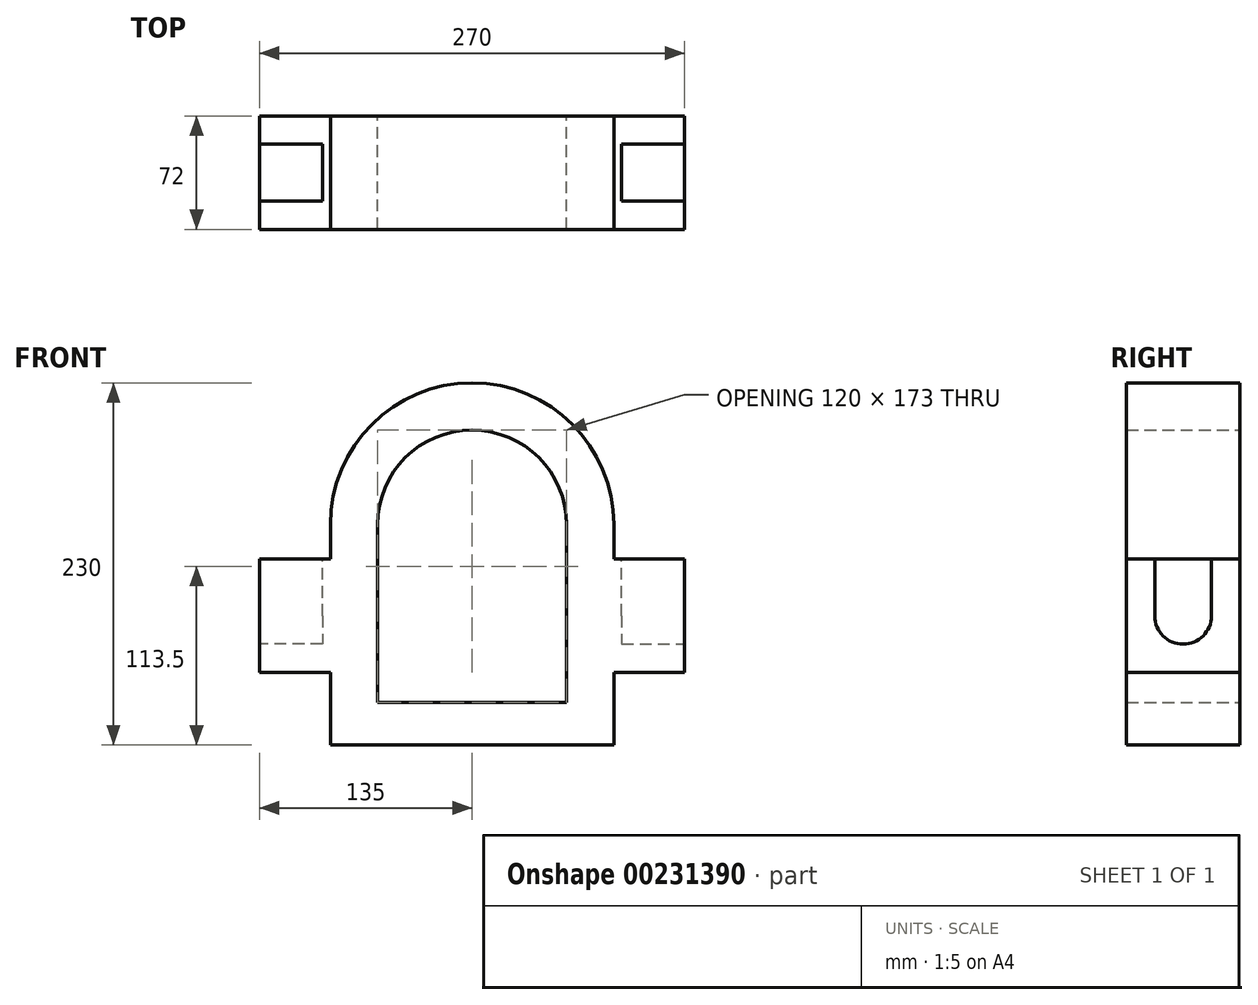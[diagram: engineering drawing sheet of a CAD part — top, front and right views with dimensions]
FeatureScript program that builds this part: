
annotation { "Feature Type Name" : "Feature", "Feature Type Description" : "" }
export const myFeature = defineFeature(function(context is Context, id is Id, definition is map)
    precondition{}
    {
        {
            var Q0;
            Q0=qCreatedBy(makeId("Front.planeOp"),FACE);
            var sketch = newSketch(context, id + "F0", { "sketchPlane" : qUnion([Q0])});
            skArc(sketch, "E0", {"start": v(90, 0) * mm, "mid": v(0, 90) * mm, "end": v(-90, 0) * mm});
            skArc(sketch, "E1", {"start": v(60, 0) * mm, "mid": v(0, 60) * mm, "end": v(-60, 0) * mm});
            skLineSegment(sketch, "E2", {"start": v(-90, 0) * mm, "end": v(-90, -22) * mm});
            skLineSegment(sketch, "E3", {"start": v(-90, -22) * mm, "end": v(-135, -22) * mm});
            skLineSegment(sketch, "E4", {"start": v(-135, -22) * mm, "end": v(-135, -94) * mm});
            skLineSegment(sketch, "E5", {"start": v(-135, -94) * mm, "end": v(-90, -94) * mm});
            skLineSegment(sketch, "E6", {"start": v(-90, -94) * mm, "end": v(-90, -140) * mm});
            skLineSegment(sketch, "E7.MirrorCS", {"start": v(90, 0) * mm, "end": v(90, -22) * mm});
            skLineSegment(sketch, "E8.MirrorCS", {"start": v(90, -22) * mm, "end": v(135, -22) * mm});
            skLineSegment(sketch, "E9.MirrorCS", {"start": v(135, -22) * mm, "end": v(135, -94) * mm});
            skLineSegment(sketch, "E10.MirrorCS", {"start": v(135, -94) * mm, "end": v(90, -94) * mm});
            skLineSegment(sketch, "E11.MirrorCS", {"start": v(90, -94) * mm, "end": v(90, -140) * mm});
            skLineSegment(sketch, "E12", {"start": v(-90, -140) * mm, "end": v(90, -140) * mm});
            skLineSegment(sketch, "E13", {"start": v(-60, 0) * mm, "end": v(-60, -113) * mm});
            skLineSegment(sketch, "E14", {"start": v(-60, -113) * mm, "end": v(60, -113) * mm});
            skLineSegment(sketch, "E15", {"start": v(60, -113) * mm, "end": v(60, 0) * mm});
            skSolve(sketch);
        }
        {
            var Q0;
            Q0=qSketchRegion(id+"F0",true);
            extrude(context, id + "F1", {"entities" : qUnion([Q0]), "endBound" : BoundingType.SYMMETRIC, "depth" : 72 * mm});
        }
        {
            var Q0;
            Q0=makeQuery(id+"F1.opExtrude","SWEPT_FACE",FACE,{"disambiguationData":[OSD([sQuery(id+"F0.wireOp",EDGE,"E8.MirrorCS")])]});
            var sketch = newSketch(context, id + "F2", { "sketchPlane" : qUnion([Q0])});
            skLineSegment(sketch, "E16", {"start": v(135, 18) * mm, "end": v(95, 18) * mm});
            skLineSegment(sketch, "E17", {"start": v(95, 18) * mm, "end": v(95, -18) * mm});
            skLineSegment(sketch, "E18", {"start": v(95, -18) * mm, "end": v(135, -18) * mm});
            skLineSegment(sketch, "E19", {"start": v(135, -18) * mm, "end": v(135, 18) * mm});
            skLineSegment(sketch, "E20.MirrorCS", {"start": v(-135, 18) * mm, "end": v(-95, 18) * mm});
            skLineSegment(sketch, "E21.MirrorCS", {"start": v(-95, -18) * mm, "end": v(-135, -18) * mm});
            skLineSegment(sketch, "E22.MirrorCS", {"start": v(-95, 18) * mm, "end": v(-95, -18) * mm});
            skLineSegment(sketch, "E23.MirrorCS", {"start": v(-135, -18) * mm, "end": v(-135, 18) * mm});
            skSolve(sketch);
        }
        {
            var Q0;
            Q0=makeQuery(id+"F1.opExtrude","SWEPT_FACE",FACE,{"disambiguationData":[OSD([sQuery(id+"F0.wireOp",EDGE,"E9.MirrorCS")])]});
            var sketch = newSketch(context, id + "F3", { "sketchPlane" : qUnion([Q0])});
            skArc(sketch, "E24", {"start": v(-18, -58) * mm, "mid": v(0, -76) * mm, "end": v(18, -58) * mm});
            skLineSegment(sketch, "E25", {"start": v(-18, -58) * mm, "end": v(18, -58) * mm});
            skSolve(sketch);
        }
        {
            var Q0;
            Q0=makeQuery(id+"F1.opExtrude","SWEPT_FACE",FACE,{"disambiguationData":[OSD([sQuery(id+"F0.wireOp",EDGE,"E4")])]});
            var sketch = newSketch(context, id + "F4", { "sketchPlane" : qUnion([Q0])});
            skLineSegment(sketch, "E26.0", {"start": v(18, -58) * mm, "end": v(-18, -58) * mm});
            skArc(sketch, "E27.0", {"start": v(18, -58) * mm, "mid": v(0, -76) * mm, "end": v(-18, -58) * mm});
            skSolve(sketch);
        }
        {
            var Q0;
            Q0=makeQuery(id+"F2.imprint","IMPRINT",FACE,{"disambiguationData":[TD([[makeQuery(id+"F2.imprint","IMPRINT",EDGE,{"derivedFrom":sQuery(id+"F2.wireOp",EDGE,"E20.MirrorCS")}),-1.0]])]});
            var Q1;
            Q1=makeQuery(id+"F2.imprint","IMPRINT",FACE,{"disambiguationData":[TD([[makeQuery(id+"F2.imprint","IMPRINT",EDGE,{"derivedFrom":sQuery(id+"F2.wireOp",EDGE,"E16")}),1.0]])]});
            extrude(context, id + "F5", {"entities" : qUnion([Q0, Q1]), "operationType" : NewBodyOperationType.REMOVE, "oppositeDirection" : true, "depth" : 36 * mm});
        }
        {
            var Q0;
            Q0=makeQuery(id+"F3.imprint","IMPRINT",FACE,{"disambiguationData":[TD([[makeQuery(id+"F3.imprint","IMPRINT",EDGE,{"derivedFrom":sQuery(id+"F3.wireOp",EDGE,"E24")}),1.0]])]});
            extrude(context, id + "F6", {"entities" : qUnion([Q0]), "operationType" : NewBodyOperationType.REMOVE, "oppositeDirection" : true, "depth" : 40 * mm});
        }
        {
            var Q0;
            Q0=makeQuery(id+"F4.imprint","IMPRINT",FACE,{"disambiguationData":[TD([[makeQuery(id+"F4.imprint","IMPRINT",EDGE,{"derivedFrom":sQuery(id+"F4.wireOp",EDGE,"E26.0")}),1.0]])]});
            extrude(context, id + "F7", {"entities" : qUnion([Q0]), "operationType" : NewBodyOperationType.REMOVE, "oppositeDirection" : true, "depth" : 40 * mm});
        }
    });
